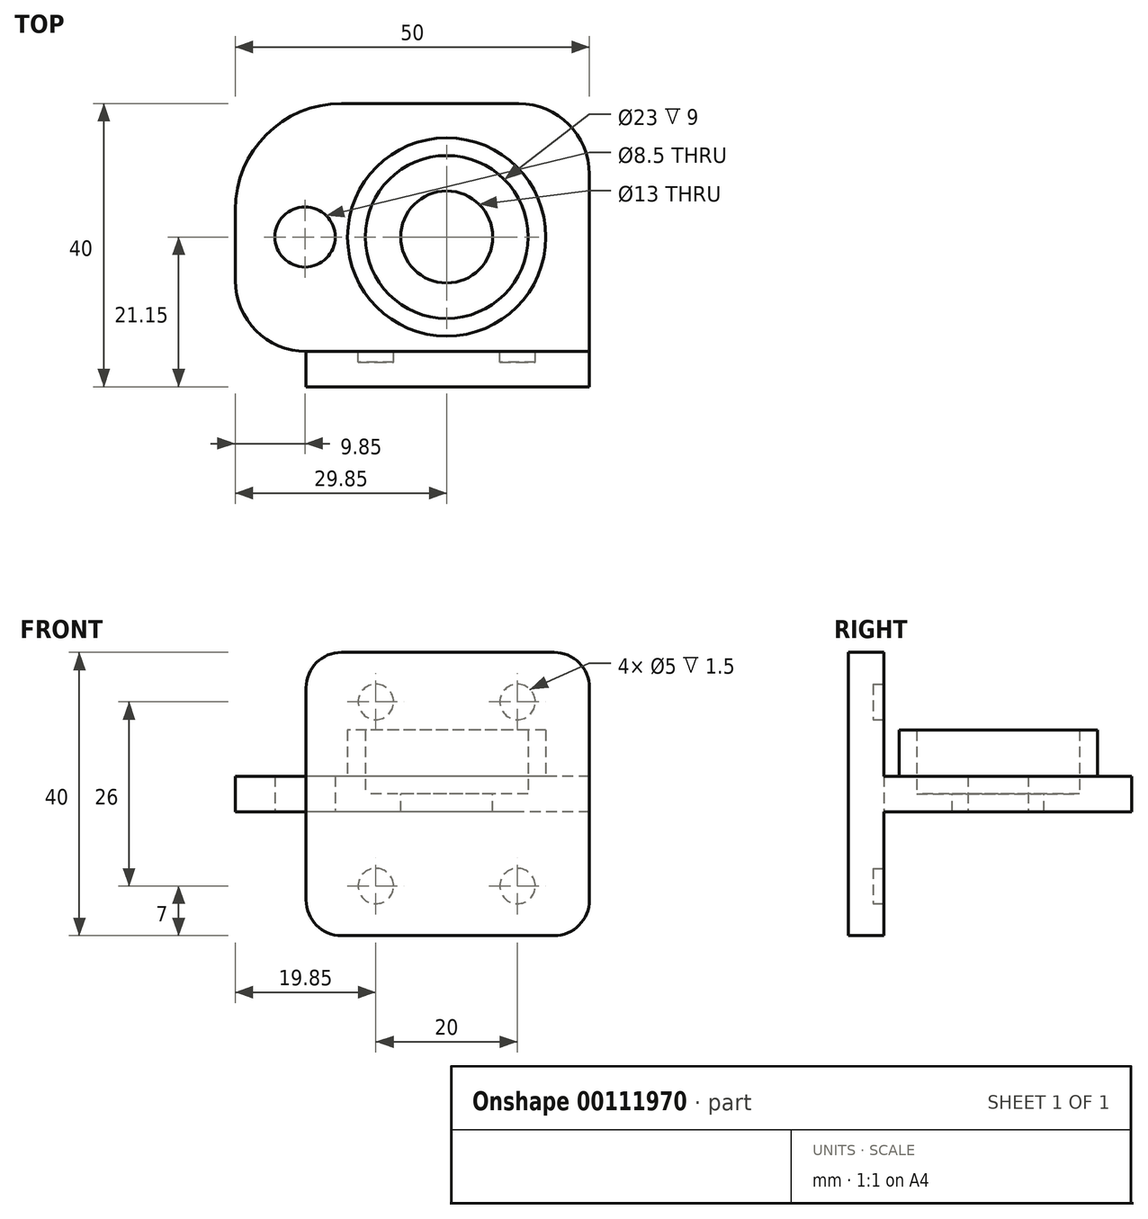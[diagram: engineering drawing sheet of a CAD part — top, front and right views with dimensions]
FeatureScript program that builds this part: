
annotation { "Feature Type Name" : "Feature", "Feature Type Description" : "" }
export const myFeature = defineFeature(function(context is Context, id is Id, definition is map)
    precondition{}
    {
        {
            var Q0;
            Q0=qCreatedBy(makeId("Top.planeOp"),FACE);
            var sketch = newSketch(context, id + "F0", { "sketchPlane" : qUnion([Q0])});
            skCircle(sketch, "E0.0", {"center": v(0, 0) * mm, "radius": 11.5 * mm});
            skCircle(sketch, "E1", {"center": v(0, 0) * mm, "radius": 14 * mm});
            skCircle(sketch, "E2", {"center": v(0, 0) * mm, "radius": 6.5 * mm});
            skCircle(sketch, "E3", {"center": v(-20, 0) * mm, "radius": 4.25 * mm});
            skLineSegment(sketch, "E4.bottom", {"start": v(0.15, -21.15) * mm, "end": v(-19.85, -21.15) * mm});
            skLineSegment(sketch, "E4.top", {"start": v(0.15, -16.15) * mm, "end": v(-19.85, -16.15) * mm});
            skLineSegment(sketch, "E4.left", {"start": v(0.15, -21.15) * mm, "end": v(0.15, -16.15) * mm});
            skLineSegment(sketch, "E4.right", {"start": v(-19.85, -21.15) * mm, "end": v(-19.85, -16.15) * mm});
            skLineSegment(sketch, "E5.bottom", {"start": v(0.15, -16.15) * mm, "end": v(20.15, -16.15) * mm});
            skLineSegment(sketch, "E5.top", {"start": v(0.15, -21.15) * mm, "end": v(20.15, -21.15) * mm});
            skLineSegment(sketch, "E5.left", {"start": v(0.15, -16.15) * mm, "end": v(0.15, -21.15) * mm});
            skLineSegment(sketch, "E5.right", {"start": v(20.15, -16.15) * mm, "end": v(20.15, -21.15) * mm});
            skLineSegment(sketch, "E6", {"start": v(20.15, -16.15) * mm, "end": v(20.15, 18.85) * mm});
            skLineSegment(sketch, "E7", {"start": v(20.15, 18.85) * mm, "end": v(-29.85, 18.85) * mm});
            skLineSegment(sketch, "E8", {"start": v(-29.85, 18.85) * mm, "end": v(-29.85, -16.15) * mm});
            skLineSegment(sketch, "E9", {"start": v(-29.85, -16.15) * mm, "end": v(-19.85, -16.15) * mm});
            skSolve(sketch);
        }
        {
            var Q0;
            Q0=makeQuery(id+"F0.imprint","IMPRINT",FACE,{"disambiguationData":[TD([[makeQuery(id+"F0.imprint","IMPRINT",EDGE,{"derivedFrom":sQuery(id+"F0.wireOp",EDGE,"E4.bottom")}),-1.0]])]});
            var Q1;
            Q1=makeQuery(id+"F0.imprint","IMPRINT",FACE,{"disambiguationData":[TD([[makeQuery(id+"F0.imprint","IMPRINT",EDGE,{"derivedFrom":sQuery(id+"F0.wireOp",EDGE,"E5.bottom")}),-1.0]])]});
            extrude(context, id + "F1", {"entities" : qUnion([Q0, Q1]), "depth" : 20 * mm});
        }
        {
            var Q0;
            Q0=makeQuery(id+"F1.opExtrude","CAP_FACE",FACE,{"disambiguationData":[OSD([sQuery(id+"F0.wireOp",EDGE,"E4.bottom"),sQuery(id+"F0.wireOp",EDGE,"E4.top"),sQuery(id+"F0.wireOp",EDGE,"E4.right"),sQuery(id+"F0.wireOp",EDGE,"E5.bottom"),sQuery(id+"F0.wireOp",EDGE,"E5.top"),sQuery(id+"F0.wireOp",EDGE,"E5.right")])],"isStart":true});
            extrude(context, id + "F2", {"entities" : qUnion([Q0]), "operationType" : NewBodyOperationType.ADD, "depth" : 20 * mm});
        }
        {
            var Q0;
            Q0=makeQuery(id+"F0.imprint","IMPRINT",FACE,{"disambiguationData":[TD([[makeQuery(id+"F0.imprint","IMPRINT",EDGE,{"derivedFrom":sQuery(id+"F0.wireOp",EDGE,"E0.0")}),-1.0]])]});
            extrude(context, id + "F3", {"entities" : qUnion([Q0]), "depth" : 9 * mm});
        }
        {
            var Q0;
            Q0=makeQuery(id+"F0.imprint","IMPRINT",FACE,{"disambiguationData":[TD([[makeQuery(id+"F0.imprint","IMPRINT",EDGE,{"derivedFrom":sQuery(id+"F0.wireOp",EDGE,"E1")}),-1.0]])]});
            var Q1;
            Q1=makeQuery(id+"F0.imprint","IMPRINT",FACE,{"disambiguationData":[TD([[makeQuery(id+"F0.imprint","IMPRINT",EDGE,{"derivedFrom":sQuery(id+"F0.wireOp",EDGE,"E0.0")}),-1.0]])]});
            extrude(context, id + "F4", {"entities" : qUnion([Q0, Q1]), "depth" : 2.5 * mm});
        }
        {
            var Q0;
            Q0=makeQuery(id+"F0.imprint","IMPRINT",FACE,{"disambiguationData":[TD([[makeQuery(id+"F0.imprint","IMPRINT",EDGE,{"derivedFrom":sQuery(id+"F0.wireOp",EDGE,"E1")}),-1.0]])]});
            var Q1;
            Q1=makeQuery(id+"F0.imprint","IMPRINT",FACE,{"disambiguationData":[TD([[makeQuery(id+"F0.imprint","IMPRINT",EDGE,{"derivedFrom":sQuery(id+"F0.wireOp",EDGE,"E0.0")}),-1.0]])]});
            var Q2;
            Q2=makeQuery(id+"F0.imprint","IMPRINT",FACE,{"disambiguationData":[TD([[makeQuery(id+"F0.imprint","IMPRINT",EDGE,{"derivedFrom":sQuery(id+"F0.wireOp",EDGE,"E0.0")}),1.0]])]});
            extrude(context, id + "F5", {"entities" : qUnion([Q0, Q1, Q2]), "oppositeDirection" : true, "depth" : 2.5 * mm});
        }
        {
            var Q0;
            Q0=makeQuery(id+"F5.opExtrude","SWEPT_EDGE",EDGE,{"disambiguationData":[OSD([sQuery(id+"F0.wireOp",EDGE,"E7"),sQuery(id+"F0.wireOp",EDGE,"E8")])]});
            var Q1;
            Q1=makeQuery(id+"F4.opExtrude","SWEPT_EDGE",EDGE,{"disambiguationData":[OSD([sQuery(id+"F0.wireOp",EDGE,"E7"),sQuery(id+"F0.wireOp",EDGE,"E8")])]});
            fillet(context, id + "F6", {"entities" : qUnion([Q0, Q1]), "radius" : 15 * mm, "tangentPropagation" : true, "allowEdgeOverflow" : false});
        }
        {
            var Q0;
            Q0=makeQuery(id+"F5.opExtrude","SWEPT_EDGE",EDGE,{"disambiguationData":[OSD([sQuery(id+"F0.wireOp",EDGE,"E6"),sQuery(id+"F0.wireOp",EDGE,"E7")])]});
            var Q1;
            Q1=makeQuery(id+"F4.opExtrude","SWEPT_EDGE",EDGE,{"disambiguationData":[OSD([sQuery(id+"F0.wireOp",EDGE,"E6"),sQuery(id+"F0.wireOp",EDGE,"E7")])]});
            fillet(context, id + "F7", {"entities" : qUnion([Q0, Q1]), "radius" : 10 * mm, "tangentPropagation" : true, "allowEdgeOverflow" : false});
        }
        {
            var Q0;
            Q0=makeQuery(id+"F5.opExtrude","SWEPT_EDGE",EDGE,{"disambiguationData":[OSD([sQuery(id+"F0.wireOp",EDGE,"E8"),sQuery(id+"F0.wireOp",EDGE,"E9")])]});
            var Q1;
            Q1=makeQuery(id+"F4.opExtrude","SWEPT_EDGE",EDGE,{"disambiguationData":[OSD([sQuery(id+"F0.wireOp",EDGE,"E8"),sQuery(id+"F0.wireOp",EDGE,"E9")])]});
            fillet(context, id + "F8", {"entities" : qUnion([Q0, Q1]), "radius" : 10 * mm, "tangentPropagation" : true, "allowEdgeOverflow" : false});
        }
        {
            var Q0;
            Q0=makeQuery(id+"F1.opExtrude","CAP_EDGE",EDGE,{"disambiguationData":[OSD([sQuery(id+"F0.wireOp",EDGE,"E4.right")])],"isStart":false});
            var Q1;
            Q1=makeQuery(id+"F1.opExtrude","CAP_EDGE",EDGE,{"disambiguationData":[OSD([sQuery(id+"F0.wireOp",EDGE,"E5.right")])],"isStart":false});
            var Q2;
            Q2=makeQuery(id+"F2.opExtrude","CAP_EDGE",EDGE,{"disambiguationData":[OSD([sQuery(id+"F0.wireOp",EDGE,"E5.right")])],"isStart":false});
            var Q3;
            Q3=makeQuery(id+"F2.opExtrude","CAP_EDGE",EDGE,{"disambiguationData":[OSD([sQuery(id+"F0.wireOp",EDGE,"E4.right")])],"isStart":false});
            fillet(context, id + "F9", {"entities" : qUnion([Q0, Q1, Q2, Q3]), "radius" : 5 * mm, "tangentPropagation" : true, "allowEdgeOverflow" : false});
        }
        {
            var Q0;
            Q0=makeQuery(id+"F1.opExtrude","SWEPT_BODY",BODY,{"disambiguationData":[OSD([sQuery(id+"F0.wireOp",EDGE,"E4.bottom"),sQuery(id+"F0.wireOp",EDGE,"E4.top"),sQuery(id+"F0.wireOp",EDGE,"E4.right"),sQuery(id+"F0.wireOp",EDGE,"E5.bottom"),sQuery(id+"F0.wireOp",EDGE,"E5.top"),sQuery(id+"F0.wireOp",EDGE,"E5.right")])]});
            var Q1;
            Q1=makeQuery(id+"F3.opExtrude","SWEPT_BODY",BODY,{"disambiguationData":[OSD([sQuery(id+"F0.wireOp",EDGE,"E0.0"),sQuery(id+"F0.wireOp",EDGE,"E1")])]});
            var Q2;
            Q2=makeQuery(id+"F4.opExtrude","SWEPT_BODY",BODY,{"disambiguationData":[OSD([sQuery(id+"F0.wireOp",EDGE,"E0.0"),sQuery(id+"F0.wireOp",EDGE,"E3"),sQuery(id+"F0.wireOp",EDGE,"E4.top"),sQuery(id+"F0.wireOp",EDGE,"E5.bottom"),sQuery(id+"F0.wireOp",EDGE,"E6"),sQuery(id+"F0.wireOp",EDGE,"E7"),sQuery(id+"F0.wireOp",EDGE,"E8"),sQuery(id+"F0.wireOp",EDGE,"E9")])]});
            var Q3;
            Q3=makeQuery(id+"F5.opExtrude","SWEPT_BODY",BODY,{"disambiguationData":[OSD([sQuery(id+"F0.wireOp",EDGE,"E2"),sQuery(id+"F0.wireOp",EDGE,"E3"),sQuery(id+"F0.wireOp",EDGE,"E4.top"),sQuery(id+"F0.wireOp",EDGE,"E5.bottom"),sQuery(id+"F0.wireOp",EDGE,"E6"),sQuery(id+"F0.wireOp",EDGE,"E7"),sQuery(id+"F0.wireOp",EDGE,"E8"),sQuery(id+"F0.wireOp",EDGE,"E9")])]});
            booleanBodies(context, id + "F10", {"operationType" : BooleanOperationType.UNION, "tools" : qUnion([Q0, Q1, Q2, Q3])});
        }
        {
            var Q0;
            {var subQ3=sQuery(id+"F0.wireOp",EDGE,"E4.right");var subQ4=sQuery(id+"F0.wireOp",EDGE,"E5.bottom");var subQ5=sQuery(id+"F0.wireOp",EDGE,"E4.top");Q0=makeQuery(id+"F10.opBoolean","SPLIT",FACE,{"disambiguationData":[TD([makeQuery(id+"F9.opFillet","BLEND_FACE",FACE,{"disambiguationData":[OSD([subQ3]),TDD([makeQuery(id+"F1.opExtrude","CAP_EDGE",EDGE,{"disambiguationData":[OSD([subQ3])],"isStart":false})])]})])],"derivedFrom":makeQuery(id+"F2.boolean.opBoolean","MERGE",FACE,{"derivedFrom":[makeQuery(id+"F1.opExtrude","SWEPT_FACE",FACE,{"disambiguationData":[OSD([subQ5,subQ4])]}),makeQuery(id+"F2.opExtrude","SWEPT_FACE",FACE,{"disambiguationData":[OSD([subQ5,subQ4])]})]})});}
            var sketch = newSketch(context, id + "F11", { "sketchPlane" : qUnion([Q0])});
            skCircle(sketch, "E10", {"center": v(-10, 13) * mm, "radius": 2.5 * mm});
            skCircle(sketch, "E11", {"center": v(10, 13) * mm, "radius": 2.5 * mm});
            skCircle(sketch, "E12", {"center": v(-10, -13) * mm, "radius": 2.5 * mm});
            skCircle(sketch, "E13", {"center": v(10, -13) * mm, "radius": 2.5 * mm});
            skSolve(sketch);
        }
        {
            var Q0;
            Q0 = qSketchRegion(id + "F11", true);
            extrude(context, id + "F12", {"entities" : qUnion([Q0]), "operationType" : NewBodyOperationType.REMOVE, "oppositeDirection" : true, "depth" : 1.5 * mm});
        }
    });
